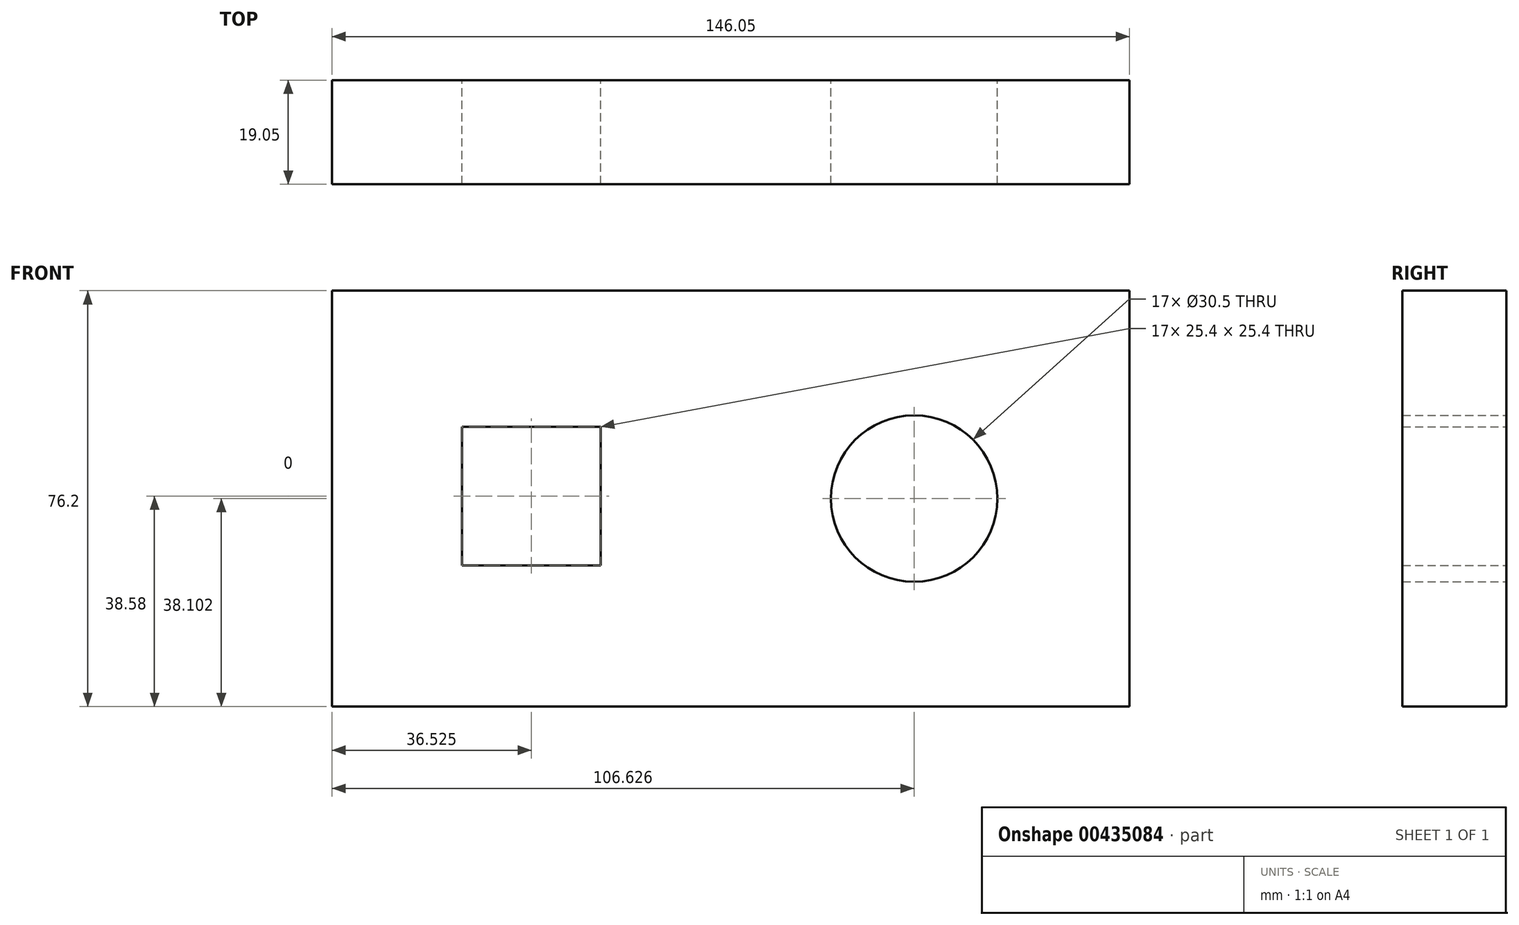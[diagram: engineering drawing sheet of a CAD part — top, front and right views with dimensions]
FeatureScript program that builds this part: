
annotation { "Feature Type Name" : "Feature", "Feature Type Description" : "" }
export const myFeature = defineFeature(function(context is Context, id is Id, definition is map)
    precondition{}
    {
        {
            var Q0;
            Q0=qCreatedBy(makeId("Front.planeOp"),FACE);
            var sketch = newSketch(context, id + "F0", { "sketchPlane" : qUnion([Q0])});
            skLineSegment(sketch, "E0.bottom", {"start": v(-74.55, 28.11) * mm, "end": v(71.5, 28.11) * mm});
            skLineSegment(sketch, "E0.top", {"start": v(-74.55, -48.09) * mm, "end": v(71.5, -48.09) * mm});
            skLineSegment(sketch, "E0.left", {"start": v(-74.55, 28.11) * mm, "end": v(-74.55, -48.09) * mm});
            skLineSegment(sketch, "E0.right", {"start": v(71.5, 28.11) * mm, "end": v(71.5, -48.09) * mm});
            skLineSegment(sketch, "E1.bottom", {"start": v(-50.72, 3.2) * mm, "end": v(-25.32, 3.2) * mm});
            skLineSegment(sketch, "E1.top", {"start": v(-50.72, -22.2) * mm, "end": v(-25.32, -22.2) * mm});
            skLineSegment(sketch, "E1.left", {"start": v(-50.72, 3.2) * mm, "end": v(-50.72, -22.2) * mm});
            skLineSegment(sketch, "E1.right", {"start": v(-25.32, 3.2) * mm, "end": v(-25.32, -22.2) * mm});
            skCircle(sketch, "E2", {"center": v(32.08, -9.99) * mm, "radius": 15.25 * mm});
            skSolve(sketch);
        }
        {
            var Q0;
            Q0 = qSketchRegion(id + "F0", true);
            extrude(context, id + "F1", {"entities" : qUnion([Q0]), "depth" : 19.05 * mm});
        }
    });
